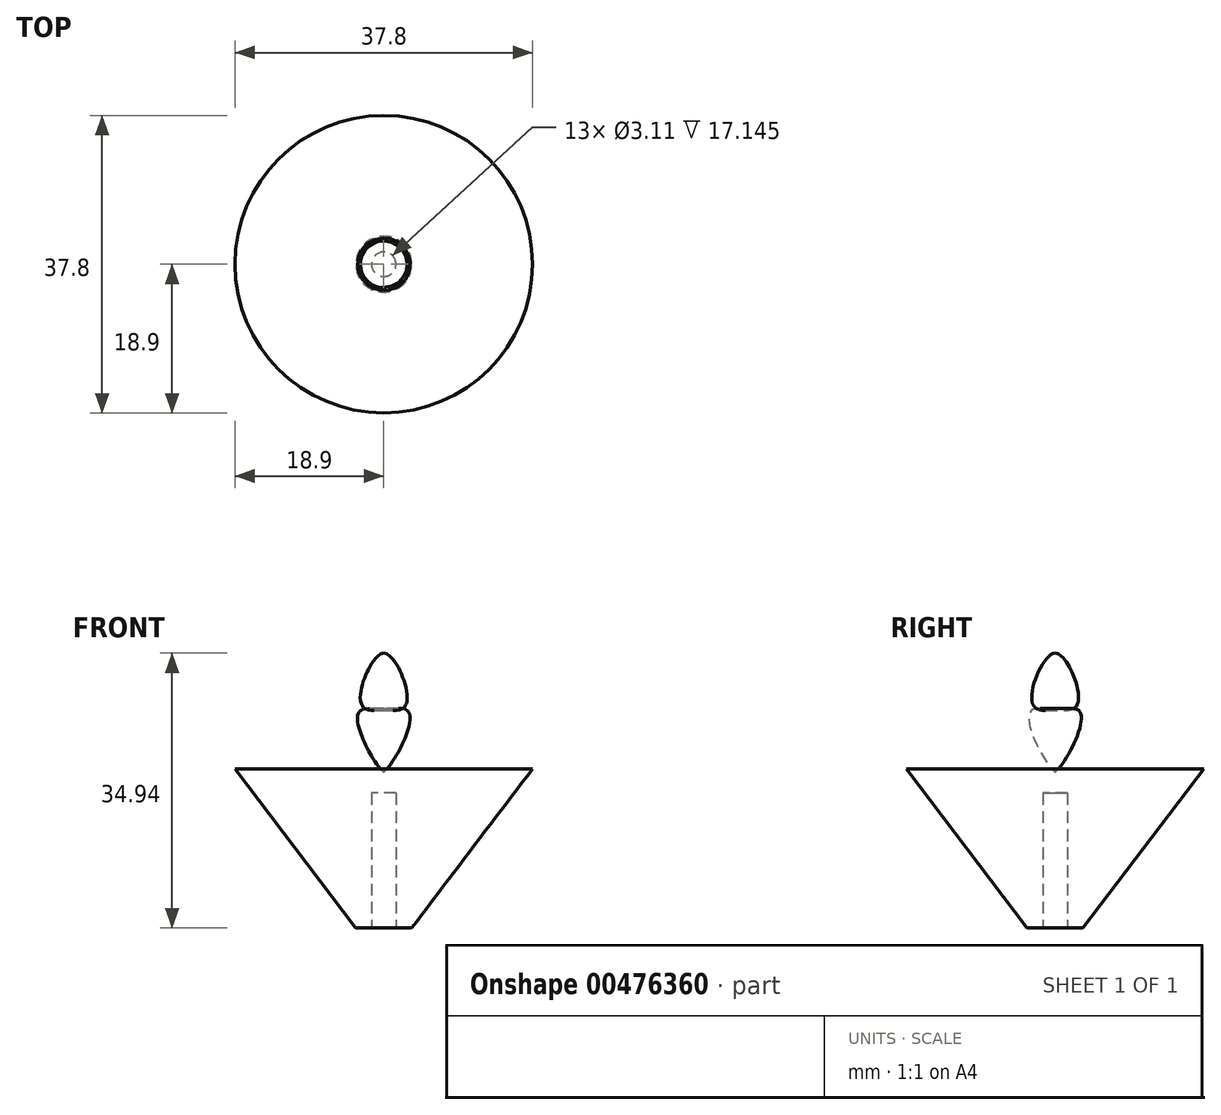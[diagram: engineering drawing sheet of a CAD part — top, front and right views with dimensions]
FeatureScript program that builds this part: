
annotation { "Feature Type Name" : "Feature", "Feature Type Description" : "" }
export const myFeature = defineFeature(function(context is Context, id is Id, definition is map)
    precondition{}
    {
        {
            var Q0;
            Q0=qCreatedBy(makeId("Front.planeOp"),FACE);
            var sketch = newSketch(context, id + "F0", { "sketchPlane" : qUnion([Q0])});
            skLineSegment(sketch, "E0", {"start": v(0, 0) * mm, "end": v(3.55, 0) * mm});
            skLineSegment(sketch, "E1", {"start": v(3.55, 0) * mm, "end": v(18.9, 20.24) * mm});
            skLineSegment(sketch, "E2", {"start": v(18.9, 20.24) * mm, "end": v(0, 20.24) * mm});
            skLineSegment(sketch, "E3", {"start": v(0, 20.24) * mm, "end": v(0, 0) * mm});
            skSolve(sketch);
        }
        {
            var Q0;
            Q0 = qSketchRegion(id + "F0", true);
            var Q1;
            Q1=sQuery(id+"F0.wireOp",EDGE,"E3");
            revolve(context, id + "F1", {"entities" : qUnion([Q0]), "axis" : qUnion([Q1]), "revolveType" : RevolveType.FULL});
        }
        {
            var Q0;
            Q0=qCreatedBy(makeId("Right.planeOp"),FACE);
            var sketch = newSketch(context, id + "F2", { "sketchPlane" : qUnion([Q0])});
            skFitSpline(sketch, "E4", {"points": [v(0, 19.82) * mm, v(3.06, 27.58) * mm, v(-2.67, 28.14) * mm, v(0, 34.94) * mm], "startDerivative": vector(11.65, 9.86) * mm, "endDerivative": vector(13.55, 0.6) * mm});
            skLineSegment(sketch, "E5", {"start": v(0, 19.82) * mm, "end": v(0, 34.94) * mm});
            skSolve(sketch);
        }
        {
            var Q0;
            Q0 = qSketchRegion(id + "F2", true);
            var Q1;
            Q1=sQuery(id+"F2.wireOp",EDGE,"E5");
            revolve(context, id + "F3", {"entities" : qUnion([Q0]), "axis" : qUnion([Q1]), "revolveType" : RevolveType.FULL});
        }
        {
            var Q0;
            Q0=qCreatedBy(makeId("Top.planeOp"),FACE);
            var sketch = newSketch(context, id + "F4", { "sketchPlane" : qUnion([Q0])});
            skCircle(sketch, "E6", {"center": v(0, 0) * mm, "radius": 1.55 * mm});
            skSolve(sketch);
        }
        {
            var Q0;
            Q0 = qSketchRegion(id + "F4", true);
            extrude(context, id + "F5", {"entities" : qUnion([Q0]), "operationType" : NewBodyOperationType.REMOVE, "depth" : 17.14 * mm});
        }
    });
